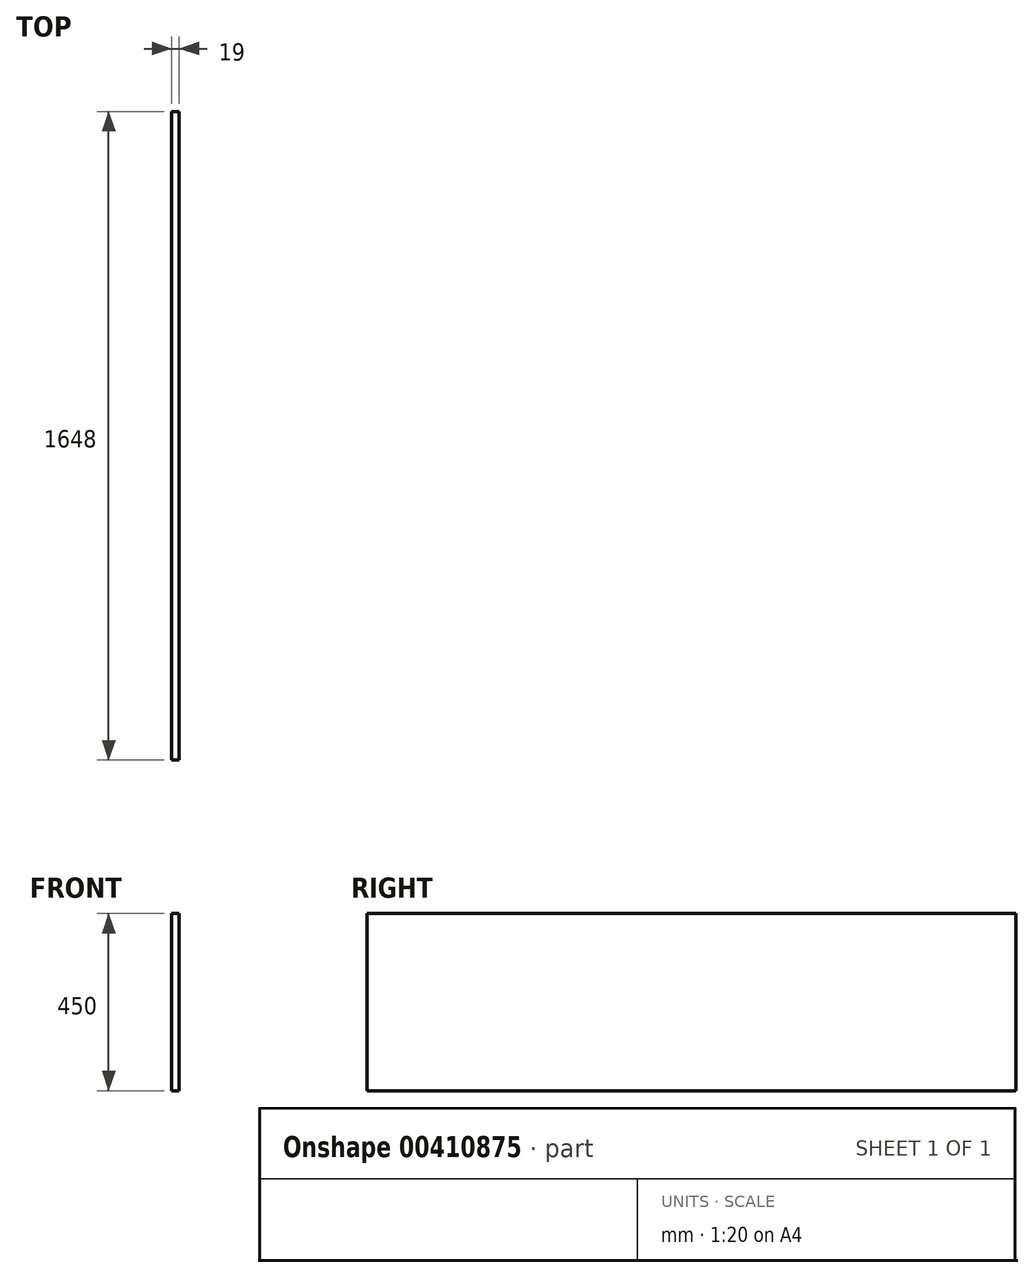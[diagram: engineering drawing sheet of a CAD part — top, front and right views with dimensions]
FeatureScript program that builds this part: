
annotation { "Feature Type Name" : "Feature", "Feature Type Description" : "" }
export const myFeature = defineFeature(function(context is Context, id is Id, definition is map)
    precondition{}
    {
        {
            var Q0;
            Q0=qCreatedBy(makeId("Top.planeOp"),FACE);
            var sketch = newSketch(context, id + "F0", { "sketchPlane" : qUnion([Q0])});
            skLineSegment(sketch, "E0.bottom", {"start": v(61.63, -827.7) * mm, "end": v(80.63, -827.7) * mm});
            skLineSegment(sketch, "E0.top", {"start": v(61.63, 820.3) * mm, "end": v(80.63, 820.3) * mm});
            skLineSegment(sketch, "E0.left", {"start": v(61.63, -827.7) * mm, "end": v(61.63, 820.3) * mm});
            skLineSegment(sketch, "E0.right", {"start": v(80.63, -827.7) * mm, "end": v(80.63, 820.3) * mm});
            skSolve(sketch);
        }
        {
            var Q0;
            Q0 = qSketchRegion(id + "F0", true);
            extrude(context, id + "F1", {"entities" : qUnion([Q0]), "depth" : 450 * mm});
        }
    });
